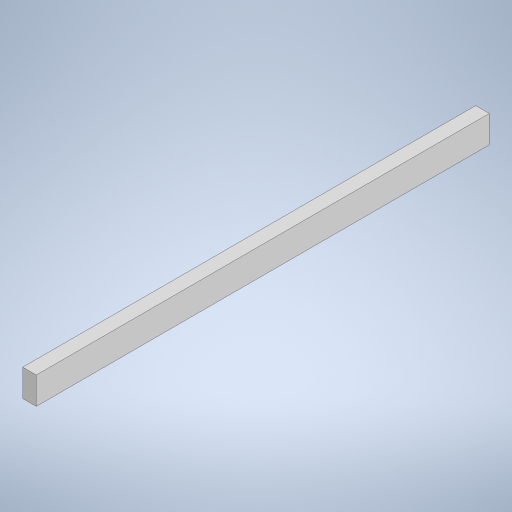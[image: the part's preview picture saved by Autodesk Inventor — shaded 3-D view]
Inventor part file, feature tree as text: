
AUTODESK INVENTOR PART (.ipt)
format: ipt  version: 2023 (Build 270158000, 158)  size: 229,888 bytes
history: native  units: mm
features: extrude x1, sketch x1
ambient origin geometry x8: Origin, YZ Plane, XZ Plane, XY Plane, X Axis, Y Axis, Z Axis, Center Point
bodies: Solid1 (feature_tree)
feature tree (2):
  extrude  "Extrusion1"  Depth=15.0mm
  sketch  "Sketch1"  dims[d0=30.0mm d1=15.0mm d2=410.0mm d3=0.0mm]
